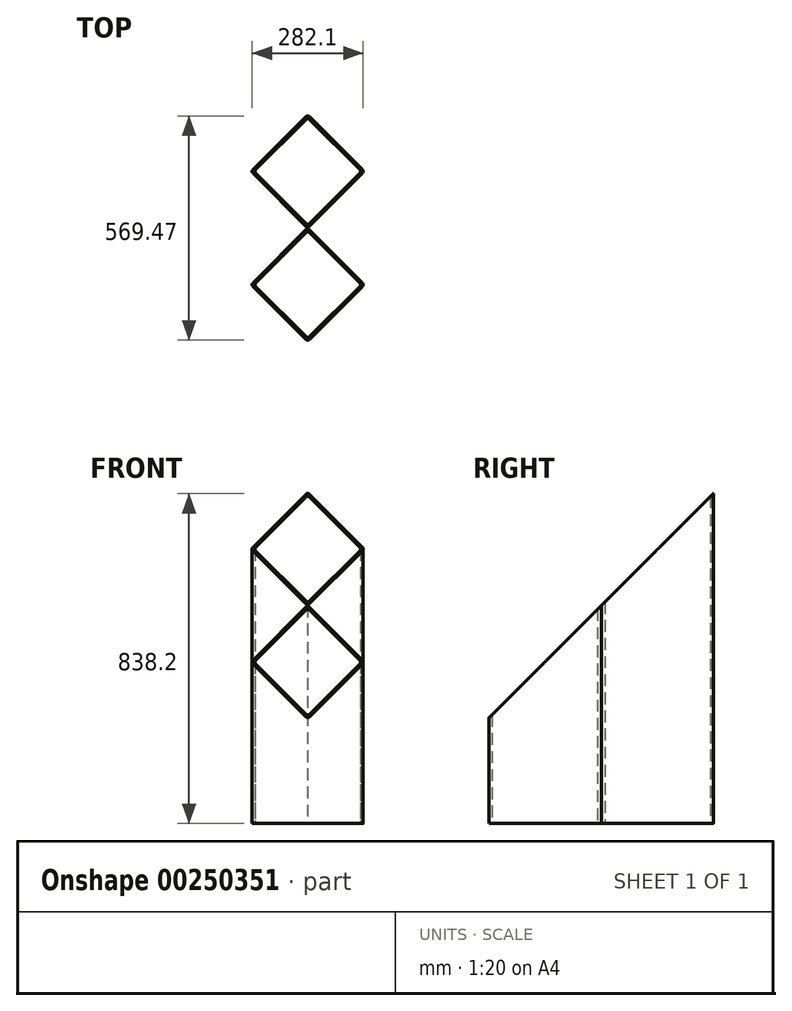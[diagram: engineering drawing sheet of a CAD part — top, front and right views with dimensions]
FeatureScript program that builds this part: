
annotation { "Feature Type Name" : "Feature", "Feature Type Description" : "" }
export const myFeature = defineFeature(function(context is Context, id is Id, definition is map)
    precondition{}
    {
        {
            var Q0;
            Q0=qCreatedBy(makeId("Top.planeOp"),FACE);
            var sketch = newSketch(context, id + "F0", { "sketchPlane" : qUnion([Q0])});
            skPoint(sketch, "E0.middle", {"position": v(0, 0) * mm});
            skLineSegment(sketch, "E1", {"start": v(-139.2, 4.5) * mm, "end": v(-4.5, 139.2) * mm});
            skLineSegment(sketch, "E2", {"start": v(4.5, 139.2) * mm, "end": v(139.2, 4.5) * mm});
            skLineSegment(sketch, "E3", {"start": v(139.2, -4.5) * mm, "end": v(0, -143.68) * mm});
            skLineSegment(sketch, "E4", {"start": v(0, -143.68) * mm, "end": v(-139.2, -4.5) * mm});
            skPoint(sketch, "E5.orphan", {"position": v(-101.6, 101.6) * mm});
            skPoint(sketch, "E6.orphan", {"position": v(-101.6, -101.6) * mm});
            skPoint(sketch, "E7.orphan", {"position": v(101.6, -101.6) * mm});
            skPoint(sketch, "E0.left.start.orphan", {"position": v(101.6, 101.6) * mm});
            skLineSegment(sketch, "E8", {"start": v(0, -143.68) * mm, "end": v(-139.2, -282.88) * mm});
            skLineSegment(sketch, "E9", {"start": v(-139.2, -291.86) * mm, "end": v(-4.5, -426.56) * mm});
            skLineSegment(sketch, "E10", {"start": v(4.5, -426.56) * mm, "end": v(139.2, -291.86) * mm});
            skLineSegment(sketch, "E11", {"start": v(139.2, -282.88) * mm, "end": v(0, -143.68) * mm});
            skLineSegment(sketch, "E12.0", {"start": v(-132.46, 4.5) * mm, "end": v(-4.5, 132.46) * mm});
            skLineSegment(sketch, "E12.1", {"start": v(-4.5, -132.46) * mm, "end": v(-132.46, -4.5) * mm});
            skLineSegment(sketch, "E12.2", {"start": v(132.46, -4.5) * mm, "end": v(4.5, -132.46) * mm});
            skLineSegment(sketch, "E12.3", {"start": v(4.5, 132.46) * mm, "end": v(132.46, 4.5) * mm});
            skLineSegment(sketch, "E13.0", {"start": v(-4.5, -154.9) * mm, "end": v(-132.46, -282.88) * mm});
            skLineSegment(sketch, "E13.1", {"start": v(132.46, -282.88) * mm, "end": v(4.5, -154.9) * mm});
            skLineSegment(sketch, "E13.2", {"start": v(4.5, -419.83) * mm, "end": v(132.46, -291.86) * mm});
            skLineSegment(sketch, "E13.3", {"start": v(-132.46, -291.86) * mm, "end": v(-4.5, -419.83) * mm});
            skPoint(sketch, "E14.visualSharp", {"position": v(-143.68, -287.37) * mm});
            skArc(sketch, "E14.filletArc", {"start": v(-139.2, -282.88) * mm, "mid": v(-141.05, -287.37) * mm, "end": v(-139.2, -291.86) * mm});
            skPoint(sketch, "E15.visualSharp", {"position": v(-136.95, -287.37) * mm});
            skArc(sketch, "E15.filletArc", {"start": v(-132.46, -282.88) * mm, "mid": v(-134.32, -287.37) * mm, "end": v(-132.46, -291.86) * mm});
            skPoint(sketch, "E16.visualSharp", {"position": v(0, -431.05) * mm});
            skArc(sketch, "E16.filletArc", {"start": v(-4.5, -426.56) * mm, "mid": v(0, -428.42) * mm, "end": v(4.5, -426.56) * mm});
            skPoint(sketch, "E17.visualSharp", {"position": v(0, -424.32) * mm});
            skArc(sketch, "E17.filletArc", {"start": v(-4.5, -419.83) * mm, "mid": v(0, -421.69) * mm, "end": v(4.5, -419.83) * mm});
            skPoint(sketch, "E18.visualSharp", {"position": v(136.95, -287.37) * mm});
            skArc(sketch, "E18.filletArc", {"start": v(132.46, -291.86) * mm, "mid": v(134.32, -287.37) * mm, "end": v(132.46, -282.88) * mm});
            skPoint(sketch, "E19.visualSharp", {"position": v(143.68, -287.37) * mm});
            skArc(sketch, "E19.filletArc", {"start": v(139.2, -291.86) * mm, "mid": v(141.05, -287.37) * mm, "end": v(139.2, -282.88) * mm});
            skPoint(sketch, "E20.visualSharp", {"position": v(0, -150.42) * mm});
            skArc(sketch, "E20.filletArc", {"start": v(4.5, -154.9) * mm, "mid": v(0, -153.05) * mm, "end": v(-4.5, -154.9) * mm});
            skPoint(sketch, "E21.visualSharp", {"position": v(0, -136.95) * mm});
            skArc(sketch, "E21.filletArc", {"start": v(-4.5, -132.46) * mm, "mid": v(0, -134.32) * mm, "end": v(4.5, -132.46) * mm});
            skPoint(sketch, "E22.visualSharp", {"position": v(143.68, 0) * mm});
            skArc(sketch, "E22.filletArc", {"start": v(139.2, -4.5) * mm, "mid": v(141.05, 0) * mm, "end": v(139.2, 4.5) * mm});
            skPoint(sketch, "E23.visualSharp", {"position": v(136.95, 0) * mm});
            skArc(sketch, "E23.filletArc", {"start": v(132.46, -4.5) * mm, "mid": v(134.32, 0) * mm, "end": v(132.46, 4.5) * mm});
            skPoint(sketch, "E24.visualSharp", {"position": v(-143.68, 0) * mm});
            skArc(sketch, "E24.filletArc", {"start": v(-139.2, 4.5) * mm, "mid": v(-141.05, 0) * mm, "end": v(-139.2, -4.5) * mm});
            skPoint(sketch, "E25.visualSharp", {"position": v(-136.95, 0) * mm});
            skArc(sketch, "E25.filletArc", {"start": v(-132.46, 4.5) * mm, "mid": v(-134.32, 0) * mm, "end": v(-132.46, -4.5) * mm});
            skPoint(sketch, "E26.visualSharp", {"position": v(0, 136.95) * mm});
            skArc(sketch, "E26.filletArc", {"start": v(4.5, 132.46) * mm, "mid": v(0, 134.32) * mm, "end": v(-4.5, 132.46) * mm});
            skPoint(sketch, "E27.visualSharp", {"position": v(0, 143.68) * mm});
            skArc(sketch, "E27.filletArc", {"start": v(4.5, 139.2) * mm, "mid": v(0, 141.05) * mm, "end": v(-4.5, 139.2) * mm});
            skSolve(sketch);
        }
        {
            var Q0;
            Q0=makeQuery(id+"F0.imprint","IMPRINT",FACE,{"disambiguationData":[TD([[makeQuery(id+"F0.imprint","IMPRINT",EDGE,{"derivedFrom":sQuery(id+"F0.wireOp",EDGE,"E1")}),-1.0]])]});
            var Q1;
            Q1=makeQuery(id+"F0.imprint","IMPRINT",FACE,{"disambiguationData":[TD([[makeQuery(id+"F0.imprint","IMPRINT",EDGE,{"derivedFrom":sQuery(id+"F0.wireOp",EDGE,"E8")}),1.0]])]});
            extrude(context, id + "F1", {"entities" : qUnion([Q0, Q1]), "depth" : 838.2 * mm});
        }
        {
            var Q0;
            Q0=qCreatedBy(makeId("Right.planeOp"),FACE);
            var sketch = newSketch(context, id + "F2", { "sketchPlane" : qUnion([Q0])});
            skLineSegment(sketch, "E28", {"start": v(140.78, 838.2) * mm, "end": v(-494.22, 838.2) * mm});
            skLineSegment(sketch, "E29", {"start": v(-494.22, 838.2) * mm, "end": v(-494.22, 203.2) * mm});
            skLineSegment(sketch, "E30", {"start": v(-494.22, 203.2) * mm, "end": v(140.78, 838.2) * mm});
            skSolve(sketch);
        }
        {
            var Q0;
            Q0 = qSketchRegion(id + "F2", true);
            extrude(context, id + "F3", {"entities" : qUnion([Q0]), "operationType" : NewBodyOperationType.REMOVE, "endBound" : BoundingType.THROUGH_ALL, "oppositeDirection" : true, "depth" : 152.4 * mm, "hasSecondDirection" : true, "secondDirectionBound" : SecondDirectionBoundingType.THROUGH_ALL, "secondDirectionOppositeDirection" : false, "secondDirectionDepth" : 152.4 * mm});
        }
    });
